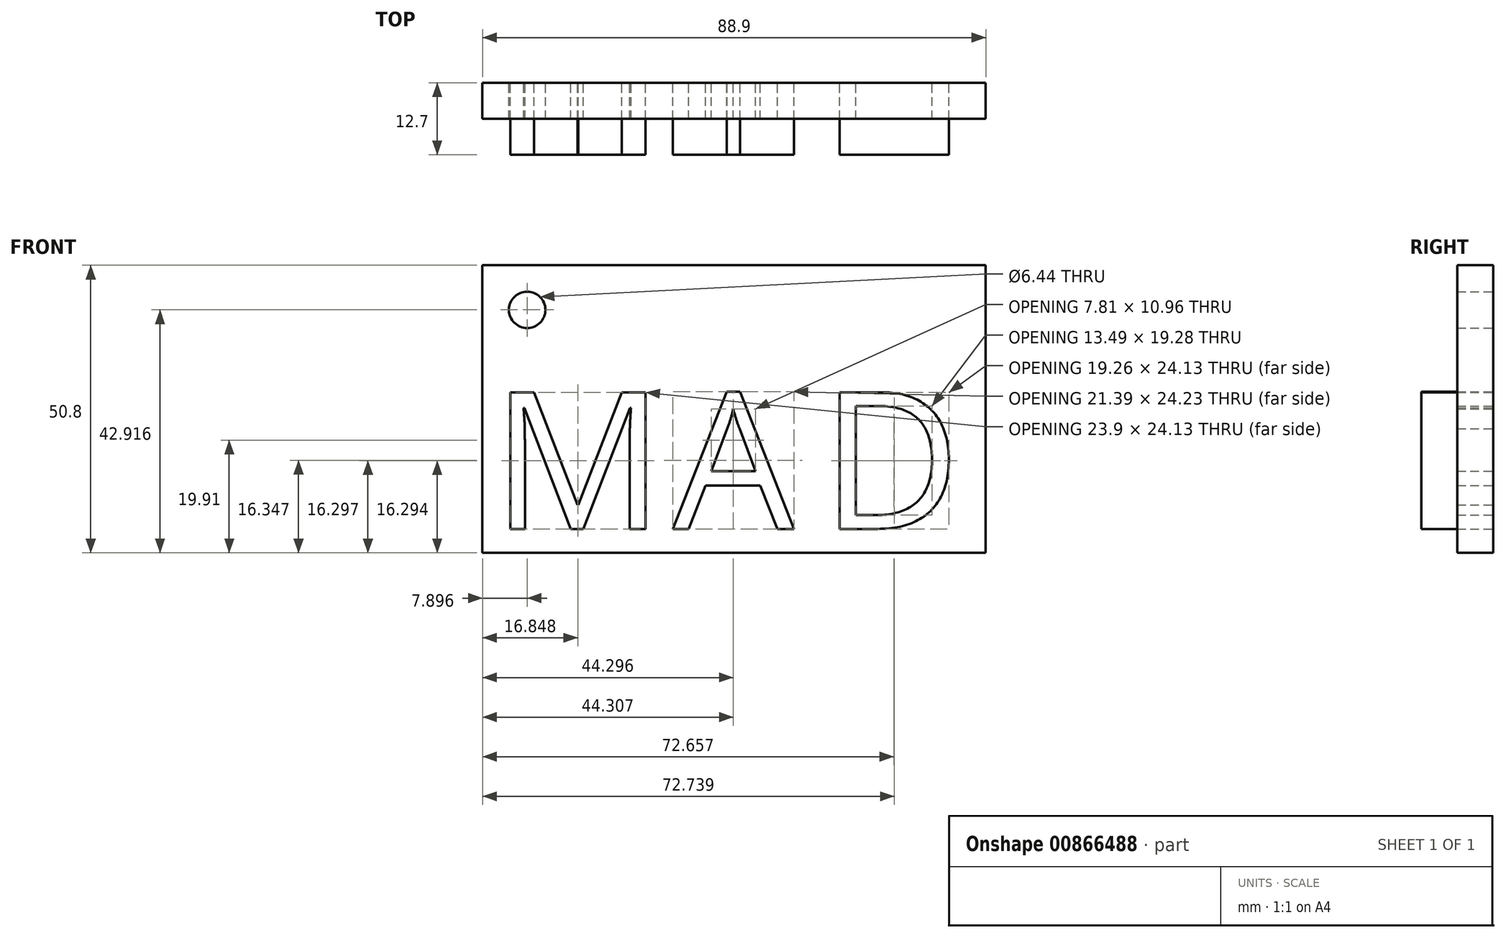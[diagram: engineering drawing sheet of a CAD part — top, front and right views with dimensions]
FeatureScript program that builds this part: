
annotation { "Feature Type Name" : "Feature", "Feature Type Description" : "" }
export const myFeature = defineFeature(function(context is Context, id is Id, definition is map)
    precondition{}
    {
        {
            var Q0;
            Q0=qCreatedBy(makeId("Front.planeOp"),FACE);
            var sketch = newSketch(context, id + "F0", { "sketchPlane" : qUnion([Q0])});
            skText(sketch, "E0", { "text": "M\n", "fontName": "OpenSans-Regular.ttf"});
            skText(sketch, "E1", { "text": "A", "fontName": "OpenSans-Regular.ttf"});
            skText(sketch, "E2", { "text": "D\n", "fontName": "OpenSans-Regular.ttf"});
            skLineSegment(sketch, "E3.bottom", {"start": v(-46.03, 33.93) * mm, "end": v(42.87, 33.93) * mm});
            skLineSegment(sketch, "E3.top", {"start": v(-46.03, -16.87) * mm, "end": v(42.87, -16.87) * mm});
            skLineSegment(sketch, "E3.left", {"start": v(-46.03, 33.93) * mm, "end": v(-46.03, -16.87) * mm});
            skLineSegment(sketch, "E3.right", {"start": v(42.87, 33.93) * mm, "end": v(42.87, -16.87) * mm});
            skCircle(sketch, "E4", {"center": v(-38.13, 26.05) * mm, "radius": 3.22 * mm});
            const initialGuessF0  = {"E0": [-0.04445, -0.01264, 1, 0, 0.02434], "E1": [-0.01243, -0.01264, 1, 0, 0.02434], "E2": [0.01376, -0.01264, 1, 0, 0.02434]};
            skSetInitialGuess(sketch, initialGuessF0);
            skSolve(sketch);
        }
        {
            var Q0;
            Q0 = qSketchRegion(id + "F0", true);
            var Q1;
            Q1=makeQuery(id+"F0.imprint","IMPRINT",FACE,{"disambiguationData":[TD([[makeQuery(id+"F0.imprint","IMPRINT",EDGE,{"derivedFrom":sQuery(id+"F0.wireOp",EDGE,"E2.sketch_text.stroke-7")}),1.0]])]});
            var Q2;
            Q2=makeQuery(id+"F0.imprint","IMPRINT",FACE,{"disambiguationData":[TD([[makeQuery(id+"F0.imprint","IMPRINT",EDGE,{"derivedFrom":sQuery(id+"F0.wireOp",EDGE,"E1.sketch_text.stroke-8")}),1.0]])]});
            extrude(context, id + "F1", {"entities" : qUnion([Q0, Q1, Q2]), "depth" : 6.35 * mm, "offsetDistance" : 25.4 * mm});
        }
        {
            var Q0;
            Q0=makeQuery(id+"F0.imprint","IMPRINT",FACE,{"disambiguationData":[TD([[makeQuery(id+"F0.imprint","IMPRINT",EDGE,{"derivedFrom":sQuery(id+"F0.wireOp",EDGE,"E2.sketch_text.stroke-0")}),-1.0]])]});
            var Q1;
            Q1=makeQuery(id+"F0.imprint","IMPRINT",FACE,{"disambiguationData":[TD([[makeQuery(id+"F0.imprint","IMPRINT",EDGE,{"derivedFrom":sQuery(id+"F0.wireOp",EDGE,"E1.sketch_text.stroke-0")}),-1.0]])]});
            var Q2;
            Q2=makeQuery(id+"F0.imprint","IMPRINT",FACE,{"disambiguationData":[TD([[makeQuery(id+"F0.imprint","IMPRINT",EDGE,{"derivedFrom":sQuery(id+"F0.wireOp",EDGE,"E0.sketch_text.stroke-0")}),-1.0]])]});
            extrude(context, id + "F2", {"entities" : qUnion([Q0, Q1, Q2]), "depth" : 12.7 * mm, "offsetDistance" : 25.4 * mm});
        }
    });
